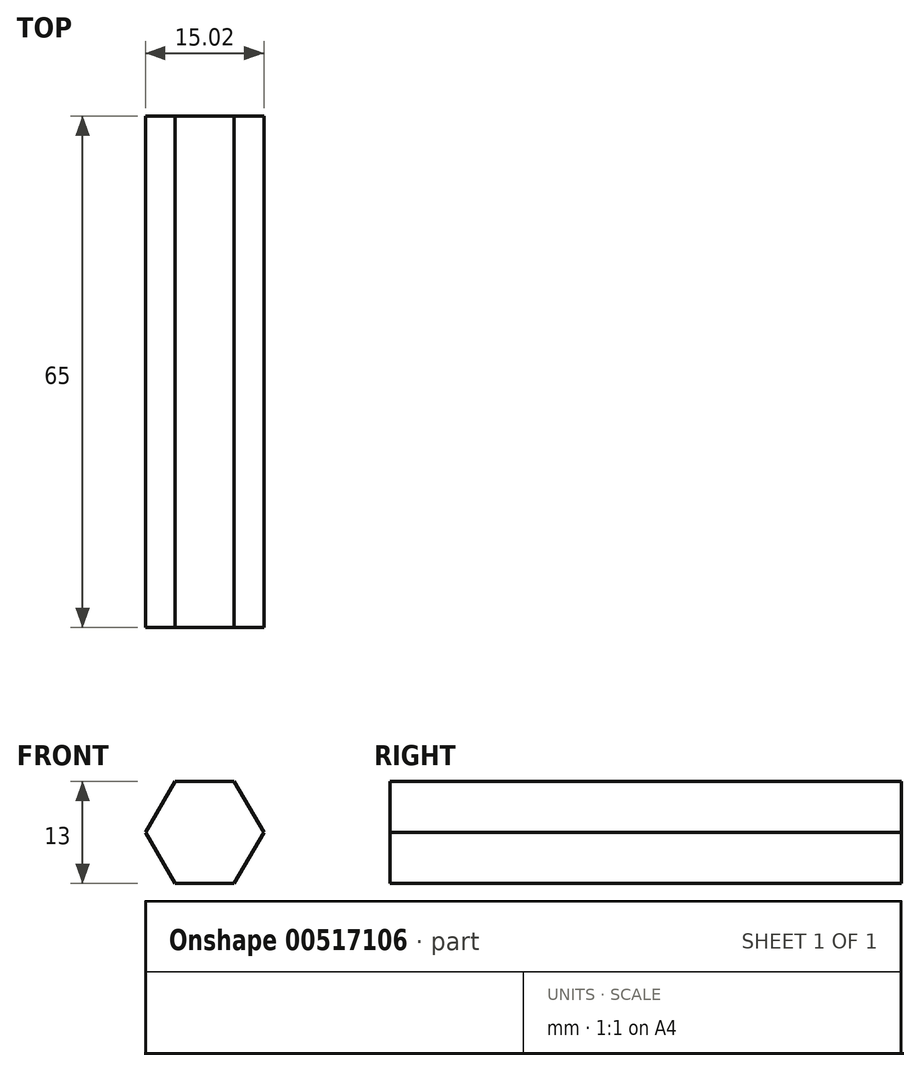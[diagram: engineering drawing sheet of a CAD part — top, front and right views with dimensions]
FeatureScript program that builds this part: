
annotation { "Feature Type Name" : "Feature", "Feature Type Description" : "" }
export const myFeature = defineFeature(function(context is Context, id is Id, definition is map)
    precondition{}
    {
        {
            var Q0;
            Q0=qCreatedBy(makeId("Front.planeOp"),FACE);
            var sketch = newSketch(context, id + "F0", { "sketchPlane" : qUnion([Q0])});
            skCircle(sketch, "E0.cCircle", {"center": v(0, 0) * mm, "radius": 6.5 * mm, "construction": true});
            skLineSegment(sketch, "E0.0", {"start": v(-3.75, 6.5) * mm, "end": v(3.75, 6.5) * mm});
            skLineSegment(sketch, "E0.1", {"start": v(3.75, 6.5) * mm, "end": v(7.5, 0) * mm});
            skLineSegment(sketch, "E0.2", {"start": v(7.5, 0) * mm, "end": v(3.75, -6.5) * mm});
            skLineSegment(sketch, "E0.3", {"start": v(3.75, -6.5) * mm, "end": v(-3.75, -6.5) * mm});
            skLineSegment(sketch, "E0.4", {"start": v(-3.75, -6.5) * mm, "end": v(-7.5, 0) * mm});
            skLineSegment(sketch, "E0.5", {"start": v(-7.5, 0) * mm, "end": v(-3.75, 6.5) * mm});
            skPoint(sketch, "E0.0.midPoint", {"position": v(0, 6.5) * mm});
            skSolve(sketch);
        }
        {
            var Q0;
            Q0 = qSketchRegion(id + "F0", true);
            extrude(context, id + "F1", {"entities" : qUnion([Q0]), "endBound" : BoundingType.SYMMETRIC, "depth" : 65 * mm, "offsetDistance" : 25 * mm});
        }
    });
